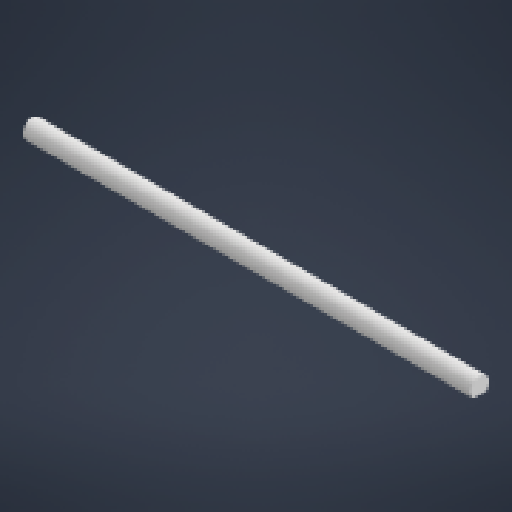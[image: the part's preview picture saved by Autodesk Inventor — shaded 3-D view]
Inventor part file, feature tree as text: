
AUTODESK INVENTOR PART (.ipt)
format: ipt  version: 2024.1 (Build 281209000, 209)  size: 131,072 bytes
history: native  units: in
note: dims shown in document units (in); Inventor stores cm internally (conversion verified against a paired STEP export)
features: extrude x1, chamfer x1, sketch x1
ambient origin geometry x8: Origin, YZ Plane, XZ Plane, XY Plane, X Axis, Y Axis, Z Axis, Center Point
bodies: Solid1 (feature_tree)
feature tree (3):
  extrude  "Extrusion1"  TaperAngle=45.0deg  [1 undecoded]
  chamfer  "Chamfer1"  Distance=5.9055in
  sketch  "Sketch1"  dims[d0=0.235in d1=45.0deg d2=5.9055in d3=0.0in d4=0.025in d5=0.125in d6=45.0deg]
note: 1 required parameter value undecoded (feature->parameter linkage not recoverable at this tier; creation-order binding heuristic only, values carry confidence <= 0.55)
